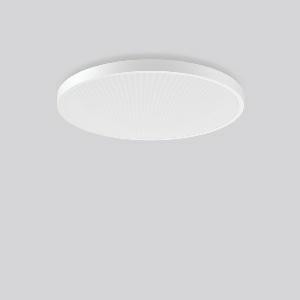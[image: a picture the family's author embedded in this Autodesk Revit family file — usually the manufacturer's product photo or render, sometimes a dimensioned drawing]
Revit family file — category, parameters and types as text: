
# Revit family: triona_round_a_312300_002_1_730_9f39
name_source: partatom
category: Lighting Fixtures
units: mm (PartAtom-declared; Revit-internal decimal feet)

## family parameters
Cut with Voids When Loaded = No
Host = Face
Light Source = No
Part Type = Normal
Room Calculation Point = No
Round Connector Dimension = Use Diameter
Shared = No

## types (1)
- TRIONA round A (1 x LED Modul 840, 11000 lm, 4000)
    Apparent Load = 103 VA
    CIE Flux Codes = 58 86 97 70 100
    Color Rendering = 80
    Color Temperature = 4000
    Default Elevation = 1800 mm
    Description = Series: TRIONA round
Decorative round LED surface-mounted luminaire. Flat, seamless frame: aluminium extrusion profile, powder coated. Cover made of sheet steel, powder-coated. Direct light emission through a diffuser plastic opal/prismatic. Indirect light emission through a flush diffuser made of satin-finish plastic. Lightguide and diffuser made of non-yellowing plastic (PMMA). Lateral light emission (RZB SIDELITE technology) for above-average homogeneous light distribution. Direct 70%, indirect 30% light emission. Suitable for Ceiling mounting, Wall (surface). Tool-free mounting via bayonet connection. Electronic ballast included. Very easy installation thanks to Plug+Play connection. With Casambi smart+free Bluetooth control for wireless network and operation using Android / iOS devices, free app available for download. Perfect for office areas (RUG < 19) and environments with computer screens in accordance with EN 12464-1. 
Colour: traffic white, matt (RAL 9016)
Diameter: 845 mm
Height: 88 mm
Lamp: LED
Socket: without socket
Colour temperature: 4000K
Colour rendering index (CRI): 80
System power: 103 W
Rated luminous flux: 11000 lm
Luminous efficiency: 107 lm/W
Control gear: Dimmable Bluetooth converter
Protection class: I
Type of protection: IP 20
    Height = 88 mm
    Lamp = 1 x LED Modul 840
    Lamp Light Flux = 11000 lm
    Lamp count = 1
    Length = 845 mm
    Lifetime = 50000 h
    Luminous efficacy = 107 lm/W
    Manufacturer = RZB
    ModVariant = No
    Model = 312300.002.1.730
    Mounting Place = Ceiling
    Mounting Type = Surface mounted
    Number of Poles = 1
    OnlyDefault = Yes
    Power Factor = 1
    Product Name = TRIONA round A
    Product group = Surface mounted modular luminaires
    ProductGroupID = 306
    Protection Class = Protection class I
    Protection Degree = IP 20
    RLX_Detail_Level = 1
    RLX_Emergency_Light_Flux = 0 lm
    RLX_Emergency_Type = 0
    RLX_Emergency_Type_DB = No
    RlxData = <blob elided: 42153 chars, md5=14d66b74>
    Socket = socket
    Standby Power = 0 W
    System Light Flux = 11000 lm
    System Power = 103 W
    Type Comments = Product without accessories
    Type Image = 312300.002.jpg
    URL = http://relux.com
    VarID = ---
    Voltage = 230 V
    Voltage Range = 220-240 V
    Weight = 0.00 kg
    Width = 0 mm  [stored 0 ft]

note: [stored X ft] marks values corroborated as IEEE doubles in the binary element streams (Revit-internal decimal feet)

## geometry (parser evidence)
native form markers: Blend x4, Sweep x12
no freeform markers — native parametric forms only
